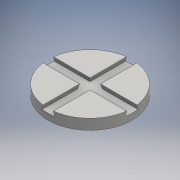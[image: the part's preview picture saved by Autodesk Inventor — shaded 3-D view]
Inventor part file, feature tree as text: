
AUTODESK INVENTOR PART (.ipt)
format: ipt  version: 2016 (Build 200138000, 138)  size: 114,688 bytes
history: native  units: mm
features: extrude x2, sketch x2, pattern_circular x1
ambient origin geometry x8: Origin, YZ Plane, XZ Plane, XY Plane, X Axis, Y Axis, Z Axis, Center Point
bodies: Solid1 (feature_tree)
feature tree (5):
  extrude  "Extrusion1"  Depth=25.0mm
  extrude  "Extrusion2"  Depth=10.0mm
  pattern_circular  "Circular Pattern1"  Count=2 Angle=90.0deg
  sketch  "Sketch1"  dims[d1=25.0mm d2=0.0mm d3=200.0mm]
  sketch  "Sketch2"  dims[d4=25.0mm d5=10.0mm d6=2.094395mm d7=20.0mm d8=90.0deg]
